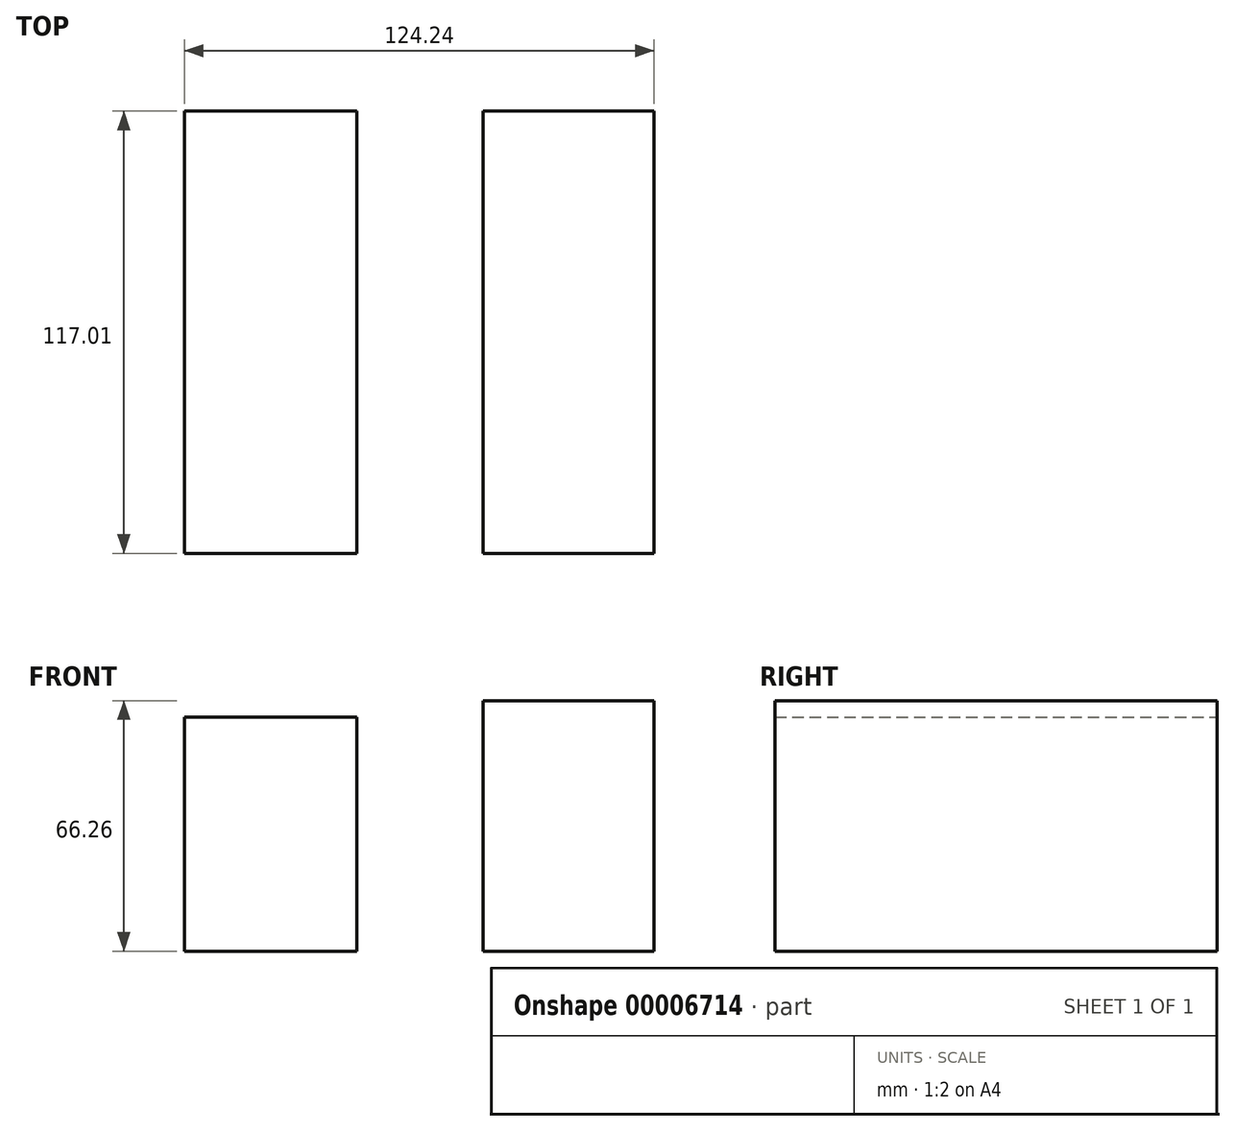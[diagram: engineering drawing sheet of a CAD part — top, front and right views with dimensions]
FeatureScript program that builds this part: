
annotation { "Feature Type Name" : "Feature", "Feature Type Description" : "" }
export const myFeature = defineFeature(function(context is Context, id is Id, definition is map)
    precondition{}
    {
        {
            var Q0;
            Q0=qCreatedBy(makeId("Front.planeOp"),FACE);
            var sketch = newSketch(context, id + "F0", { "sketchPlane" : qUnion([Q0])});
            skLineSegment(sketch, "E0.bottom", {"start": v(-62.34, 39.07) * mm, "end": v(-16.68, 39.07) * mm});
            skLineSegment(sketch, "E0.top", {"start": v(-62.34, -22.81) * mm, "end": v(-16.68, -22.81) * mm});
            skLineSegment(sketch, "E0.left", {"start": v(-62.34, 39.07) * mm, "end": v(-62.34, -22.81) * mm});
            skLineSegment(sketch, "E0.right", {"start": v(-16.68, 39.07) * mm, "end": v(-16.68, -22.81) * mm});
            skLineSegment(sketch, "E1.bottom", {"start": v(16.68, 43.45) * mm, "end": v(61.9, 43.45) * mm});
            skLineSegment(sketch, "E1.top", {"start": v(16.68, -22.81) * mm, "end": v(61.9, -22.81) * mm});
            skLineSegment(sketch, "E1.left", {"start": v(16.68, 43.45) * mm, "end": v(16.68, -22.81) * mm});
            skLineSegment(sketch, "E1.right", {"start": v(61.9, 43.45) * mm, "end": v(61.9, -22.81) * mm});
            skSolve(sketch);
        }
        {
            var Q0;
            Q0 = qSketchRegion(id + "F0", true);
            extrude(context, id + "F1", {"entities" : qUnion([Q0]), "depth" : 117.01 * mm});
        }
    });
